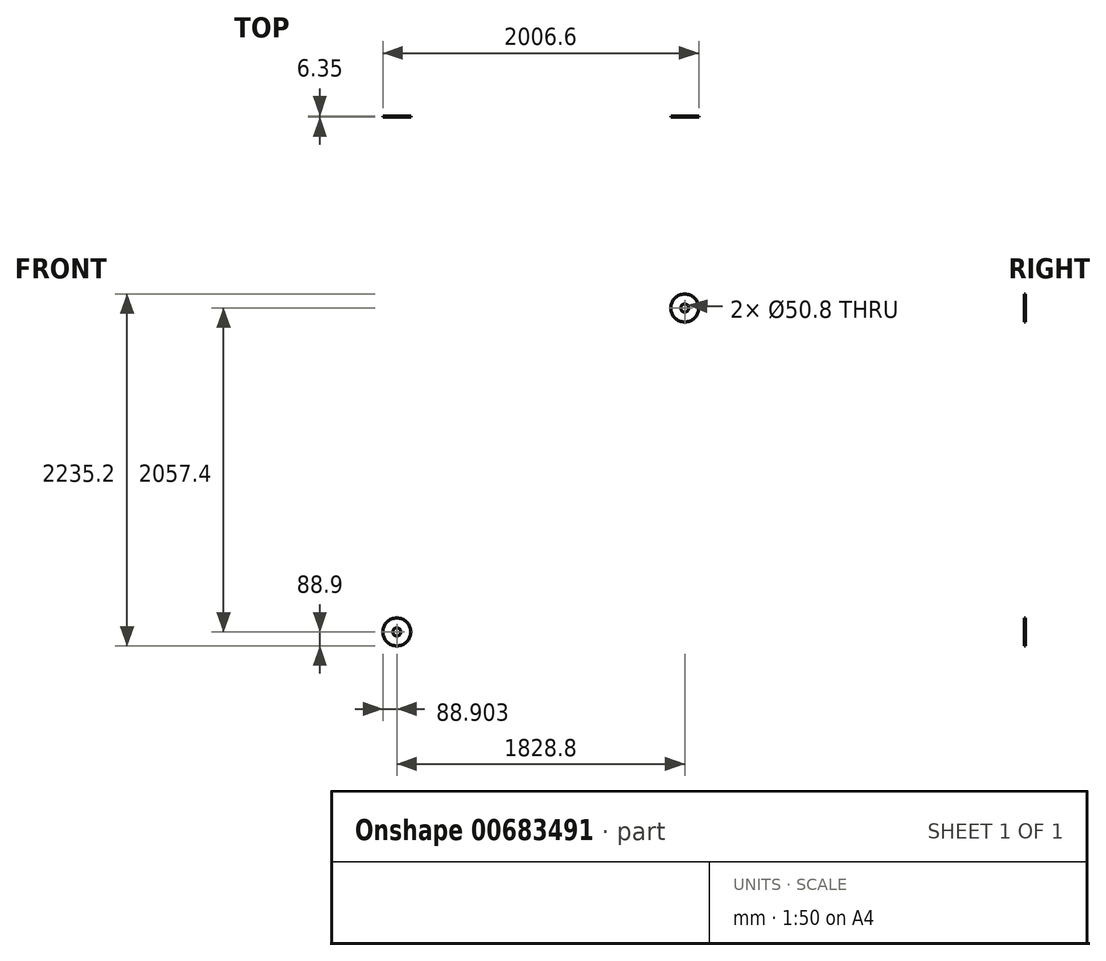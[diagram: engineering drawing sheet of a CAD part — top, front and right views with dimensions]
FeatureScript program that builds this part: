
annotation { "Feature Type Name" : "Feature", "Feature Type Description" : "" }
export const myFeature = defineFeature(function(context is Context, id is Id, definition is map)
    precondition{}
    {
        {
            var Q0;
            Q0=qCreatedBy(makeId("Top.planeOp"),FACE);
            var sketch = newSketch(context, id + "F0", { "sketchPlane" : qUnion([Q0])});
            skLineSegment(sketch, "E0", {"start": v(-414.26, 89.96) * mm, "end": v(-414.26, 166.16) * mm});
            skLineSegment(sketch, "E1", {"start": v(42.94, 89.96) * mm, "end": v(42.94, 166.16) * mm});
            skLineSegment(sketch, "E2", {"start": v(-642.2, 166.16) * mm, "end": v(429.4, 166.16) * mm, "construction": true});
            skArc(sketch, "E3", {"start": v(-414.26, 166.16) * mm, "mid": v(-185.66, 394.76) * mm, "end": v(42.94, 166.16) * mm});
            skLineSegment(sketch, "E4", {"start": v(-185.66, 166.16) * mm, "end": v(-185.66, 524.23) * mm, "construction": true});
            skPoint(sketch, "E5", {"position": v(-185.66, 394.76) * mm});
            skLineSegment(sketch, "E6", {"start": v(-414.26, 89.96) * mm, "end": v(-414.26, -291.04) * mm});
            skArc(sketch, "E7.1.0.1", {"start": v(42.94, 166.16) * mm, "mid": v(271.54, 394.76) * mm, "end": v(500.14, 166.16) * mm, "construction": true});
            skLineSegment(sketch, "E7.1.0.2", {"start": v(500.14, 89.96) * mm, "end": v(500.14, 166.16) * mm, "construction": true});
            skLineSegment(sketch, "E7.2.0.0", {"start": v(500.14, 89.96) * mm, "end": v(500.14, 166.16) * mm, "construction": true});
            skArc(sketch, "E7.2.0.1", {"start": v(500.14, 166.16) * mm, "mid": v(728.74, 394.76) * mm, "end": v(957.34, 166.16) * mm, "construction": true});
            skLineSegment(sketch, "E7.2.0.2", {"start": v(957.34, 89.96) * mm, "end": v(957.34, 166.16) * mm, "construction": true});
            skLineSegment(sketch, "E7.3.0.0", {"start": v(957.34, 89.96) * mm, "end": v(957.34, 166.16) * mm, "construction": true});
            skArc(sketch, "E7.3.0.1", {"start": v(957.34, 166.16) * mm, "mid": v(1185.94, 394.76) * mm, "end": v(1414.54, 166.16) * mm, "construction": true});
            skLineSegment(sketch, "E7.3.0.2", {"start": v(1414.54, 89.96) * mm, "end": v(1414.54, 166.16) * mm, "construction": true});
            skLineSegment(sketch, "E7.direction1", {"start": v(-414.26, 89.96) * mm, "end": v(42.94, 89.96) * mm, "construction": true});
            skSolve(sketch);
        }
        {
            var Q0;
            Q0=qCreatedBy(makeId("Top.planeOp"),FACE);
            cPlane(context, id + "F1", {"entities" : qUnion([Q0]), "cplaneType" : CPlaneType.OFFSET, "offset" : 685.8 * mm, "width" : 152.4 * mm, "height" : 152.4 * mm});
        }
        {
            var Q0;
            Q0=qCreatedBy(id+"F1.planeOp",FACE);
            cPlane(context, id + "F2", {"entities" : qUnion([Q0]), "cplaneType" : CPlaneType.OFFSET, "offset" : 685.8 * mm, "width" : 152.4 * mm, "height" : 152.4 * mm});
        }
        {
            var Q0;
            Q0=qCreatedBy(id+"F2.planeOp",FACE);
            cPlane(context, id + "F3", {"entities" : qUnion([Q0]), "cplaneType" : CPlaneType.OFFSET, "offset" : 685.8 * mm, "width" : 152.4 * mm, "height" : 152.4 * mm});
        }
        {
            var Q0;
            Q0=qCreatedBy(id+"F1.planeOp",FACE);
            var sketch = newSketch(context, id + "F4", { "sketchPlane" : qUnion([Q0])});
            skLineSegment(sketch, "E8.0", {"start": v(500.14, 89.96) * mm, "end": v(500.14, 166.16) * mm});
            skArc(sketch, "E9.0", {"start": v(42.94, 166.16) * mm, "mid": v(271.54, 394.76) * mm, "end": v(500.14, 166.16) * mm});
            skLineSegment(sketch, "E10.0", {"start": v(42.94, 89.96) * mm, "end": v(42.94, 166.16) * mm});
            skSolve(sketch);
        }
        {
            var Q0;
            Q0=qCreatedBy(id+"F2.planeOp",FACE);
            var sketch = newSketch(context, id + "F5", { "sketchPlane" : qUnion([Q0])});
            skArc(sketch, "E11.0", {"start": v(500.14, 166.16) * mm, "mid": v(728.74, 394.76) * mm, "end": v(957.34, 166.16) * mm});
            skLineSegment(sketch, "E11.1", {"start": v(500.14, 89.96) * mm, "end": v(500.14, 166.16) * mm});
            skLineSegment(sketch, "E11.2", {"start": v(957.34, 89.96) * mm, "end": v(957.34, 166.16) * mm});
            skSolve(sketch);
        }
        {
            var Q0;
            Q0=qCreatedBy(id+"F3.planeOp",FACE);
            var sketch = newSketch(context, id + "F6", { "sketchPlane" : qUnion([Q0])});
            skLineSegment(sketch, "E12.0", {"start": v(957.34, 89.96) * mm, "end": v(957.34, 166.16) * mm});
            skArc(sketch, "E12.1", {"start": v(957.34, 166.16) * mm, "mid": v(1185.94, 394.76) * mm, "end": v(1414.54, 166.16) * mm});
            skLineSegment(sketch, "E12.2", {"start": v(1414.54, 89.96) * mm, "end": v(1414.54, 166.16) * mm});
            skLineSegment(sketch, "E13", {"start": v(1414.54, 89.96) * mm, "end": v(1414.54, -291.04) * mm});
            skLineSegment(sketch, "E14", {"start": v(957.34, 89.96) * mm, "end": v(957.34, -291.04) * mm, "construction": true});
            skSolve(sketch);
        }
        {
            var Q0;
            Q0=sQuery(id+"F6.wireOp",VERTEX,"E12.1.start");
            var Q1;
            Q1=sQuery(id+"F6.wireOp",VERTEX,"E12.0.start");
            var Q2;
            Q2=sQuery(id+"F5.wireOp",VERTEX,"E11.2.start");
            cPlane(context, id + "F7", {"entities" : qUnion([Q0, Q1, Q2]), "cplaneType" : CPlaneType.THREE_POINT, "offset" : 25.4 * mm, "width" : 152.4 * mm, "height" : 152.4 * mm});
        }
        {
            var Q0;
            Q0=sQuery(id+"F5.wireOp",VERTEX,"E11.1.end");
            var Q1;
            Q1=sQuery(id+"F5.wireOp",VERTEX,"E11.1.start");
            var Q2;
            Q2=sQuery(id+"F4.wireOp",VERTEX,"E8.0.start");
            cPlane(context, id + "F8", {"entities" : qUnion([Q0, Q1, Q2]), "cplaneType" : CPlaneType.THREE_POINT, "offset" : 25.4 * mm, "width" : 152.4 * mm, "height" : 152.4 * mm});
        }
        {
            var Q0;
            Q0=sQuery(id+"F4.wireOp",VERTEX,"E10.0.end");
            var Q1;
            Q1=sQuery(id+"F4.wireOp",VERTEX,"E10.0.start");
            var Q2;
            Q2=sQuery(id+"F0.wireOp",VERTEX,"E1.start");
            cPlane(context, id + "F9", {"entities" : qUnion([Q0, Q1, Q2]), "cplaneType" : CPlaneType.THREE_POINT, "offset" : 25.4 * mm, "width" : 152.4 * mm, "height" : 152.4 * mm});
        }
        {
            var Q0;
            Q0=qCreatedBy(id+"F7.planeOp",FACE);
            var sketch = newSketch(context, id + "F10", { "sketchPlane" : qUnion([Q0])});
            skPoint(sketch, "E15.0", {"position": v(-89.96, 2057.4) * mm});
            skPoint(sketch, "E16.0", {"position": v(-89.96, 1371.6) * mm});
            skArc(sketch, "E17", {"start": v(164.04, 1803.4) * mm, "mid": v(89.65, 1983) * mm, "end": v(-89.96, 2057.4) * mm});
            skLineSegment(sketch, "E18", {"start": v(164.04, 1803.4) * mm, "end": v(164.04, 1625.6) * mm});
            skArc(sketch, "E19", {"start": v(-89.96, 1371.6) * mm, "mid": v(89.65, 1446) * mm, "end": v(164.04, 1625.6) * mm});
            skArc(sketch, "E20.0.1.0", {"start": v(164.04, 1117.6) * mm, "mid": v(89.65, 1297.2) * mm, "end": v(-89.96, 1371.6) * mm, "construction": true});
            skLineSegment(sketch, "E20.0.1.1", {"start": v(164.04, 1117.6) * mm, "end": v(164.04, 939.8) * mm, "construction": true});
            skArc(sketch, "E20.0.1.2", {"start": v(-89.96, 685.8) * mm, "mid": v(89.65, 760.2) * mm, "end": v(164.04, 939.8) * mm, "construction": true});
            skArc(sketch, "E20.0.2.0", {"start": v(164.04, 431.8) * mm, "mid": v(89.65, 611.4) * mm, "end": v(-89.96, 685.8) * mm, "construction": true});
            skLineSegment(sketch, "E20.0.2.1", {"start": v(164.04, 431.8) * mm, "end": v(164.04, 254) * mm, "construction": true});
            skArc(sketch, "E20.0.2.2", {"start": v(-89.96, 0) * mm, "mid": v(89.65, 74.4) * mm, "end": v(164.04, 254) * mm, "construction": true});
            skLineSegment(sketch, "E20.direction1", {"start": v(-89.96, 1803.4) * mm, "end": v(-64.56, 1803.4) * mm, "construction": true});
            skLineSegment(sketch, "E20.direction2", {"start": v(-89.96, 1803.4) * mm, "end": v(-89.96, 1117.6) * mm, "construction": true});
            skSolve(sketch);
        }
        {
            var Q0;
            Q0=qCreatedBy(id+"F8.planeOp",FACE);
            var sketch = newSketch(context, id + "F11", { "sketchPlane" : qUnion([Q0])});
            skArc(sketch, "E21.0", {"start": v(164.04, 1117.6) * mm, "mid": v(89.65, 1297.2) * mm, "end": v(-89.96, 1371.6) * mm});
            skLineSegment(sketch, "E22.0", {"start": v(164.04, 1117.6) * mm, "end": v(164.04, 939.8) * mm});
            skArc(sketch, "E23.0", {"start": v(-89.96, 685.8) * mm, "mid": v(89.65, 760.2) * mm, "end": v(164.04, 939.8) * mm});
            skSolve(sketch);
        }
        {
            var Q0;
            Q0=qCreatedBy(id+"F9.planeOp",FACE);
            var sketch = newSketch(context, id + "F12", { "sketchPlane" : qUnion([Q0])});
            skArc(sketch, "E24.0", {"start": v(164.04, 431.8) * mm, "mid": v(89.65, 611.4) * mm, "end": v(-89.96, 685.8) * mm});
            skLineSegment(sketch, "E24.1", {"start": v(164.04, 431.8) * mm, "end": v(164.04, 254) * mm});
            skArc(sketch, "E24.2", {"start": v(-89.96, 0) * mm, "mid": v(89.65, 74.4) * mm, "end": v(164.04, 254) * mm});
            skSolve(sketch);
        }
        {
            var Q0;
            Q0=sQuery(id+"F6.wireOp",VERTEX,"E13.end");
            var Q1;
            Q1=sQuery(id+"F6.wireOp",VERTEX,"E14.end");
            var Q2;
            Q2=sQuery(id+"F0.wireOp",VERTEX,"E6.end");
            cPlane(context, id + "F13", {"entities" : qUnion([Q0, Q1, Q2]), "cplaneType" : CPlaneType.THREE_POINT, "offset" : 25.4 * mm, "width" : 152.4 * mm, "height" : 152.4 * mm});
        }
        {
            var Q0;
            Q0=qCreatedBy(id+"F13.planeOp",FACE);
            var sketch = newSketch(context, id + "F14", { "sketchPlane" : qUnion([Q0])});
            skPoint(sketch, "E25.0", {"position": v(-1414.54, 2057.4) * mm});
            skCircle(sketch, "E26", {"center": v(-1414.54, 2057.4) * mm, "radius": 25.4 * mm});
            skSolve(sketch);
        }
        {
            var Q0;
            Q0=qCreatedBy(id+"F13.planeOp",FACE);
            var sketch = newSketch(context, id + "F15", { "sketchPlane" : qUnion([Q0])});
            skCircle(sketch, "E27.0", {"center": v(-1414.54, 2057.4) * mm, "radius": 25.4 * mm});
            skCircle(sketch, "E28", {"center": v(-1414.54, 2057.4) * mm, "radius": 88.9 * mm});
            skCircle(sketch, "E29.0", {"center": v(414.26, 0) * mm, "radius": 25.4 * mm});
            skCircle(sketch, "E30", {"center": v(414.26, 0) * mm, "radius": 88.9 * mm});
            skSolve(sketch);
        }
        {
            var Q0;
            Q0 = qSketchRegion(id + "F15", true);
            extrude(context, id + "F16", {"entities" : qUnion([Q0]), "flatOperationType" : FlatOperationType.REMOVE, "depth" : 6.35 * mm, "offsetDistance" : 25.4 * mm, "domain" : OperationDomain.MODEL});
        }
    });
